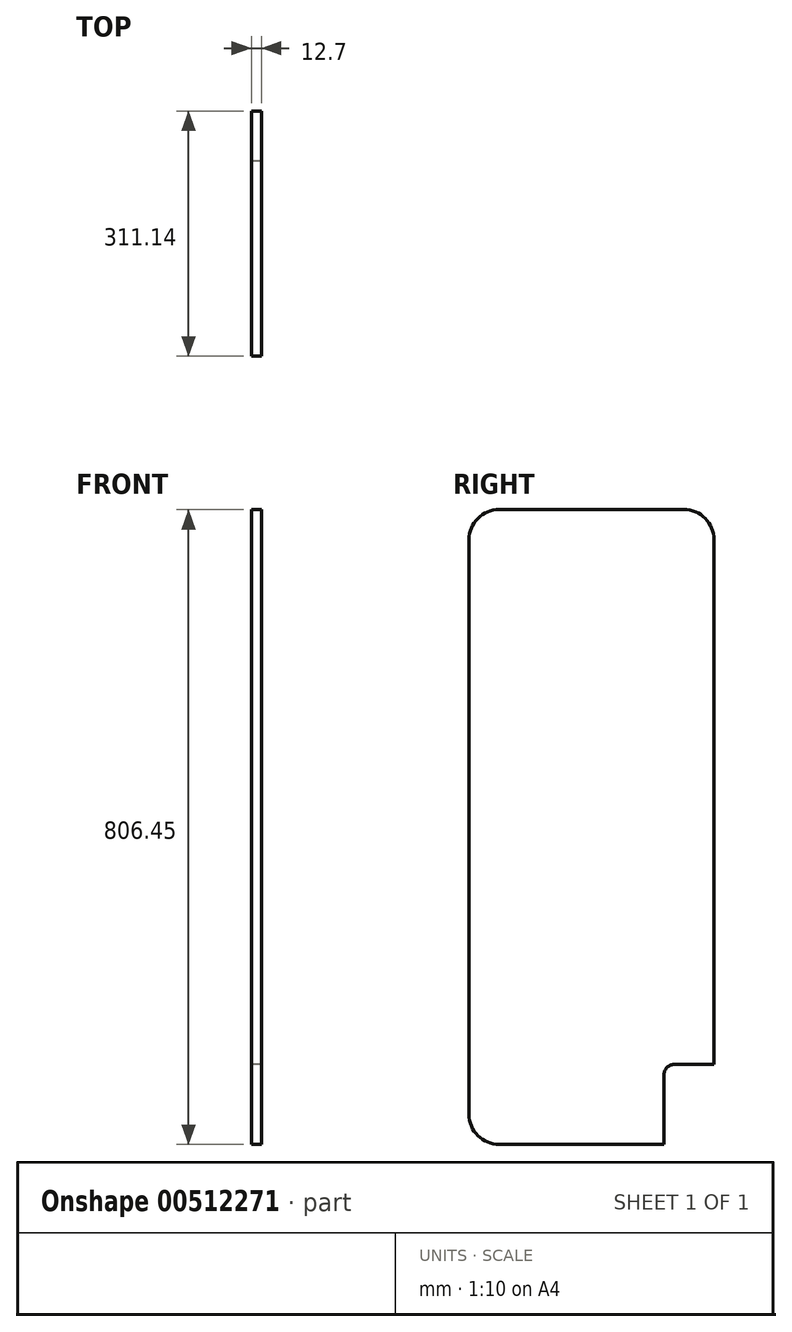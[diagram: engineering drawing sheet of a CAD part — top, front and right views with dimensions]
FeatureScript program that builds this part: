
annotation { "Feature Type Name" : "Feature", "Feature Type Description" : "" }
export const myFeature = defineFeature(function(context is Context, id is Id, definition is map)
    precondition{}
    {
        {
            var Q0;
            Q0=qCreatedBy(makeId("Right.planeOp"),FACE);
            var sketch = newSketch(context, id + "F0", { "sketchPlane" : qUnion([Q0])});
            skLineSegment(sketch, "E0.bottom", {"start": v(-155.58, 806.45) * mm, "end": v(155.58, 806.45) * mm});
            skLineSegment(sketch, "E0.top", {"start": v(-155.58, 0) * mm, "end": v(155.58, 0) * mm});
            skLineSegment(sketch, "E0.left", {"start": v(-155.57, 806.45) * mm, "end": v(-155.58, 0) * mm});
            skLineSegment(sketch, "E0.right", {"start": v(155.58, 806.45) * mm, "end": v(155.58, 0) * mm});
            skArc(sketch, "E1", {"start": v(-117.48, 806.45) * mm, "mid": v(-144.42, 795.3) * mm, "end": v(-155.58, 768.35) * mm});
            skArc(sketch, "E2", {"start": v(155.58, 768.35) * mm, "mid": v(144.42, 795.3) * mm, "end": v(117.48, 806.45) * mm});
            skArc(sketch, "E3", {"start": v(-155.58, 38.1) * mm, "mid": v(-144.42, 11.16) * mm, "end": v(-117.48, 0) * mm});
            skLineSegment(sketch, "E4", {"start": v(92.08, 0) * mm, "end": v(92.08, 101.6) * mm});
            skLineSegment(sketch, "E5", {"start": v(92.08, 101.6) * mm, "end": v(155.58, 101.6) * mm});
            skLineSegment(sketch, "E6", {"start": v(-155.58, 828.68) * mm, "end": v(155.58, 828.68) * mm});
            skLineSegment(sketch, "E7", {"start": v(-155.58, -85.73) * mm, "end": v(155.58, -85.72) * mm});
            skSolve(sketch);
        }
        {
            var Q0;
            {var subQ3=sQuery(id+"F0.wireOp",EDGE,"E1");Q0=makeQuery(id+"F0.imprint","IMPRINT",FACE,{"disambiguationData":[TD([[makeQuery(id+"F0.imprint","IMPRINT",EDGE,{"derivedFrom":subQ3}),1.0]])]});}
            extrude(context, id + "F1", {"entities" : qUnion([Q0]), "depth" : 12.7 * mm});
        }
        {
            var Q0;
            Q0=makeQuery(id+"F1.opExtrude","SWEPT_EDGE",EDGE,{"disambiguationData":[OSD([sQuery(id+"F0.wireOp",EDGE,"E4"),sQuery(id+"F0.wireOp",EDGE,"E5")])]});
            fillet(context, id + "F2", {"entities" : qUnion([Q0]), "radius" : 12.7 * mm, "tangentPropagation" : true, "allowEdgeOverflow" : false});
        }
    });
